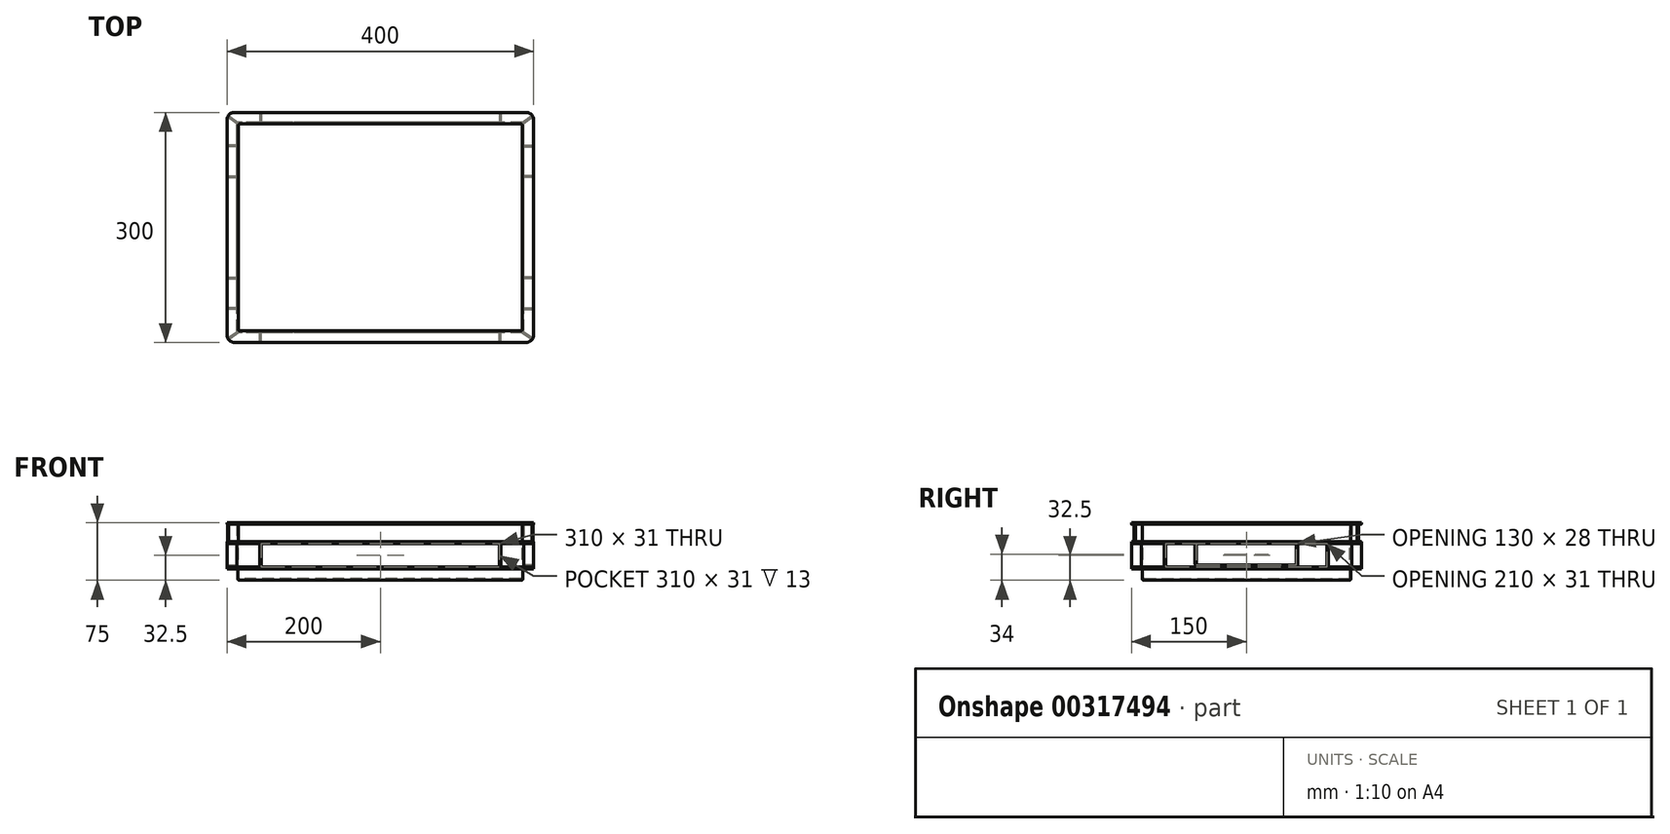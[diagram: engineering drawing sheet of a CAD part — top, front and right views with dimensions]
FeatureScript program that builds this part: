
annotation { "Feature Type Name" : "Feature", "Feature Type Description" : "" }
export const myFeature = defineFeature(function(context is Context, id is Id, definition is map)
    precondition{}
    {
        {
            var Q0;
            Q0=qCreatedBy(makeId("Top.planeOp"),FACE);
            var sketch = newSketch(context, id + "F0", { "sketchPlane" : qUnion([Q0])});
            skLineSegment(sketch, "E0.bottom", {"start": v(186, -136) * mm, "end": v(-186, -136) * mm});
            skLineSegment(sketch, "E0.top", {"start": v(186, 136) * mm, "end": v(-186, 136) * mm});
            skLineSegment(sketch, "E0.left", {"start": v(186, -136) * mm, "end": v(186, 136) * mm});
            skLineSegment(sketch, "E0.right", {"start": v(-186, -136) * mm, "end": v(-186, 136) * mm});
            skPoint(sketch, "E0.middle", {"position": v(0, 0) * mm});
            skPoint(sketch, "E1.visualSharp", {"position": v(-186, 136) * mm});
            skPoint(sketch, "E2.visualSharp", {"position": v(186, 136) * mm});
            skPoint(sketch, "E3.visualSharp", {"position": v(186, -136) * mm});
            skPoint(sketch, "E4.visualSharp", {"position": v(-186, -136) * mm});
            skSolve(sketch);
        }
        {
            var Q0;
            Q0=qSketchRegion(id+"F0",true);
            extrude(context, id + "F1", {"entities" : qUnion([Q0]), "depth" : 15 * mm});
        }
        {
            var Q0;
            Q0=makeQuery(id+"F1.opExtrude","CAP_FACE",FACE,{"disambiguationData":[OSD([sQuery(id+"F0.wireOp",EDGE,"E0.bottom"),sQuery(id+"F0.wireOp",EDGE,"E0.top"),sQuery(id+"F0.wireOp",EDGE,"E0.left"),sQuery(id+"F0.wireOp",EDGE,"E0.right")])],"isStart":false});
            var sketch = newSketch(context, id + "F2", { "sketchPlane" : qUnion([Q0])});
            skLineSegment(sketch, "E5.bottom", {"start": v(190, -150) * mm, "end": v(-190, -150) * mm});
            skLineSegment(sketch, "E5.top", {"start": v(190, 150) * mm, "end": v(-190, 150) * mm});
            skLineSegment(sketch, "E5.left", {"start": v(200, -140) * mm, "end": v(200, 140) * mm});
            skLineSegment(sketch, "E5.right", {"start": v(-200, -140) * mm, "end": v(-200, 140) * mm});
            skPoint(sketch, "E5.middle", {"position": v(0, 0) * mm});
            skPoint(sketch, "E6.visualSharp", {"position": v(-200, 150) * mm});
            skArc(sketch, "E6.filletArc", {"start": v(-190, 150) * mm, "mid": v(-197.07, 147.07) * mm, "end": v(-200, 140) * mm});
            skPoint(sketch, "E7.visualSharp", {"position": v(200, 150) * mm});
            skArc(sketch, "E7.filletArc", {"start": v(200, 140) * mm, "mid": v(197.07, 147.07) * mm, "end": v(190, 150) * mm});
            skPoint(sketch, "E8.visualSharp", {"position": v(200, -150) * mm});
            skArc(sketch, "E8.filletArc", {"start": v(190, -150) * mm, "mid": v(197.07, -147.07) * mm, "end": v(200, -140) * mm});
            skPoint(sketch, "E9.visualSharp", {"position": v(-200, -150) * mm});
            skArc(sketch, "E9.filletArc", {"start": v(-200, -140) * mm, "mid": v(-197.07, -147.07) * mm, "end": v(-190, -150) * mm});
            skSolve(sketch);
        }
        {
            var Q0;
            Q0=makeQuery(id+"F2.imprint","IMPRINT",FACE,{"disambiguationData":[TD([[makeQuery(id+"F2.imprint","IMPRINT",EDGE,{"derivedFrom":makeQuery(id+"F1.opExtrude","CAP_EDGE",EDGE,{"disambiguationData":[OSD([sQuery(id+"F0.wireOp",EDGE,"E0.bottom")])],"isStart":false})}),-1.0]])]});
            var Q1;
            Q1=makeQuery(id+"F2.imprint","IMPRINT",FACE,{"disambiguationData":[TD([[makeQuery(id+"F2.imprint","IMPRINT",EDGE,{"derivedFrom":sQuery(id+"F2.wireOp",EDGE,"E5.bottom")}),-1.0]])]});
            extrude(context, id + "F3", {"entities" : qUnion([Q0, Q1]), "operationType" : NewBodyOperationType.ADD, "depth" : 2 * mm});
        }
        {
            var Q0;
            Q0=makeQuery(id+"F3.opExtrude","CAP_FACE",FACE,{"disambiguationData":[OSD([sQuery(id+"F2.wireOp",EDGE,"E5.bottom"),sQuery(id+"F2.wireOp",EDGE,"E5.top"),sQuery(id+"F2.wireOp",EDGE,"E5.left"),sQuery(id+"F2.wireOp",EDGE,"E5.right"),sQuery(id+"F2.wireOp",EDGE,"E6.filletArc"),sQuery(id+"F2.wireOp",EDGE,"E7.filletArc"),sQuery(id+"F2.wireOp",EDGE,"E8.filletArc"),sQuery(id+"F2.wireOp",EDGE,"E9.filletArc")])],"isStart":false});
            var sketch = newSketch(context, id + "F4", { "sketchPlane" : qUnion([Q0])});
            skLineSegment(sketch, "E10.bottom", {"start": v(187, -137) * mm, "end": v(157, -137) * mm});
            skLineSegment(sketch, "E10.top", {"start": v(187, 137) * mm, "end": v(157, 137) * mm});
            skLineSegment(sketch, "E10.left", {"start": v(187, -137) * mm, "end": v(187, -107) * mm});
            skLineSegment(sketch, "E10.right", {"start": v(-187, -137) * mm, "end": v(-187, -107) * mm});
            skPoint(sketch, "E10.middle", {"position": v(0, 0) * mm});
            skLineSegment(sketch, "E11.bottom", {"start": v(-155, -150) * mm, "end": v(-157, -150) * mm});
            skLineSegment(sketch, "E11.left", {"start": v(-155, -150) * mm, "end": v(-155, -137) * mm});
            skLineSegment(sketch, "E11.right", {"start": v(-157, -150) * mm, "end": v(-157, -137) * mm});
            skPoint(sketch, "E11.middle", {"position": v(-156, -143.5) * mm});
            skLineSegment(sketch, "E12.trimOffspring", {"start": v(-157, -137) * mm, "end": v(-187, -137) * mm});
            skLineSegment(sketch, "E13.bottom", {"start": v(-187, -107) * mm, "end": v(-200, -107) * mm});
            skLineSegment(sketch, "E13.top", {"start": v(-187, -105) * mm, "end": v(-200, -105) * mm});
            skLineSegment(sketch, "E13.right", {"start": v(-200, -107) * mm, "end": v(-200, -105) * mm});
            skPoint(sketch, "E13.middle", {"position": v(-193.5, -106) * mm});
            skLineSegment(sketch, "E14.trimOffspring", {"start": v(-187, -105) * mm, "end": v(-187, 105) * mm});
            skLineSegment(sketch, "E15.MirrorCS", {"start": v(200, -107) * mm, "end": v(200, -105) * mm});
            skLineSegment(sketch, "E16.MirrorCS", {"start": v(155, -150) * mm, "end": v(155, -137) * mm});
            skLineSegment(sketch, "E17.MirrorCS", {"start": v(155, -150) * mm, "end": v(157, -150) * mm});
            skLineSegment(sketch, "E18.MirrorCS", {"start": v(157, -150) * mm, "end": v(157, -137) * mm});
            skLineSegment(sketch, "E19.MirrorCS", {"start": v(187, -105) * mm, "end": v(200, -105) * mm});
            skLineSegment(sketch, "E20.MirrorCS", {"start": v(187, -107) * mm, "end": v(200, -107) * mm});
            skPoint(sketch, "E21.MirrorP", {"position": v(193.5, -106) * mm});
            skLineSegment(sketch, "E22.trimOffspring", {"start": v(187, -105) * mm, "end": v(187, 105) * mm});
            skLineSegment(sketch, "E23.trimOffspring", {"start": v(155, -137) * mm, "end": v(-155, -137) * mm});
            skLineSegment(sketch, "E24.MirrorCS", {"start": v(-200, 107) * mm, "end": v(-200, 105) * mm});
            skPoint(sketch, "E25.MirrorP", {"position": v(-193.5, 106) * mm});
            skLineSegment(sketch, "E26.MirrorCS", {"start": v(-187, 105) * mm, "end": v(-200, 105) * mm});
            skLineSegment(sketch, "E27.MirrorCS", {"start": v(-187, 107) * mm, "end": v(-200, 107) * mm});
            skLineSegment(sketch, "E28.MirrorCS", {"start": v(-155, 150) * mm, "end": v(-157, 150) * mm});
            skLineSegment(sketch, "E29.MirrorCS", {"start": v(-157, 150) * mm, "end": v(-157, 137) * mm});
            skPoint(sketch, "E30.MirrorP", {"position": v(-156, 143.5) * mm});
            skLineSegment(sketch, "E31.MirrorCS", {"start": v(-155, 150) * mm, "end": v(-155, 137) * mm});
            skLineSegment(sketch, "E32.MirrorCS", {"start": v(155, 150) * mm, "end": v(157, 150) * mm});
            skLineSegment(sketch, "E33.MirrorCS", {"start": v(155, 150) * mm, "end": v(155, 137) * mm});
            skLineSegment(sketch, "E34.MirrorCS", {"start": v(157, 150) * mm, "end": v(157, 137) * mm});
            skLineSegment(sketch, "E35.MirrorCS", {"start": v(200, 107) * mm, "end": v(200, 105) * mm});
            skLineSegment(sketch, "E36.MirrorCS", {"start": v(187, 105) * mm, "end": v(200, 105) * mm});
            skPoint(sketch, "E37.MirrorP", {"position": v(193.5, 106) * mm});
            skLineSegment(sketch, "E38.MirrorCS", {"start": v(187, 107) * mm, "end": v(200, 107) * mm});
            skLineSegment(sketch, "E39.trimOffspring", {"start": v(-187, 107) * mm, "end": v(-187, 137) * mm});
            skLineSegment(sketch, "E40.trimOffspring", {"start": v(-157, 137) * mm, "end": v(-187, 137) * mm});
            skLineSegment(sketch, "E41.trimOffspring", {"start": v(155, 137) * mm, "end": v(-155, 137) * mm});
            skLineSegment(sketch, "E42.trimOffspring", {"start": v(187, 107) * mm, "end": v(187, 137) * mm});
            skSolve(sketch);
        }
        {
            var Q0;
            Q0=qSketchRegion(id+"F4",true);
            extrude(context, id + "F5", {"entities" : qUnion([Q0]), "operationType" : NewBodyOperationType.ADD, "depth" : ((126 - 50) - 45) * mm});
        }
        {
            var Q0;
            Q0=makeQuery(id+"F5.opExtrude","CAP_FACE",FACE,{"disambiguationData":[OSD([sQuery(id+"F4.wireOp",EDGE,"E10.bottom"),sQuery(id+"F4.wireOp",EDGE,"E10.top"),sQuery(id+"F4.wireOp",EDGE,"E10.left"),sQuery(id+"F4.wireOp",EDGE,"E10.right")])],"isStart":false});
            var sketch = newSketch(context, id + "F6", { "sketchPlane" : qUnion([Q0])});
            skArc(sketch, "E43.0", {"start": v(-190, 150) * mm, "mid": v(-197.07, 147.07) * mm, "end": v(-200, 140) * mm});
            skArc(sketch, "E43.1", {"start": v(-200, -140) * mm, "mid": v(-197.07, -147.07) * mm, "end": v(-190, -150) * mm});
            skArc(sketch, "E43.2", {"start": v(190, -150) * mm, "mid": v(197.07, -147.07) * mm, "end": v(200, -140) * mm});
            skArc(sketch, "E43.3", {"start": v(200, 140) * mm, "mid": v(197.07, 147.07) * mm, "end": v(190, 150) * mm});
            skLineSegment(sketch, "E44", {"start": v(-200, 140) * mm, "end": v(-200, -140) * mm});
            skLineSegment(sketch, "E45", {"start": v(-190, -150) * mm, "end": v(190, -150) * mm});
            skLineSegment(sketch, "E46", {"start": v(200, 140) * mm, "end": v(200, -140) * mm});
            skLineSegment(sketch, "E47", {"start": v(-190, 150) * mm, "end": v(190, 150) * mm});
            skSolve(sketch);
        }
        {
            var Q0;
            Q0=qSketchRegion(id+"F6",true);
            extrude(context, id + "F7", {"entities" : qUnion([Q0]), "operationType" : NewBodyOperationType.ADD, "depth" : 2 * mm});
        }
        {
            var Q0;
            Q0=makeQuery(id+"F7.opExtrude","CAP_FACE",FACE,{"disambiguationData":[OSD([sQuery(id+"F6.wireOp",EDGE,"E43.0"),sQuery(id+"F6.wireOp",EDGE,"E43.1"),sQuery(id+"F6.wireOp",EDGE,"E43.2"),sQuery(id+"F6.wireOp",EDGE,"E43.3"),sQuery(id+"F6.wireOp",EDGE,"E44"),sQuery(id+"F6.wireOp",EDGE,"E45"),sQuery(id+"F6.wireOp",EDGE,"E46"),sQuery(id+"F6.wireOp",EDGE,"E47")])],"isStart":false});
            var sketch = newSketch(context, id + "F8", { "sketchPlane" : qUnion([Q0])});
            skLineSegment(sketch, "E48.bottom", {"start": v(185.3, -137) * mm, "end": v(-185.3, -137) * mm});
            skLineSegment(sketch, "E48.top", {"start": v(185.3, 137) * mm, "end": v(-185.3, 137) * mm});
            skLineSegment(sketch, "E48.left", {"start": v(187, -135.76) * mm, "end": v(187, 135.76) * mm});
            skLineSegment(sketch, "E48.right", {"start": v(-187, -135.76) * mm, "end": v(-187, 135.76) * mm});
            skPoint(sketch, "E48.middle", {"position": v(0, 0) * mm});
            skLineSegment(sketch, "E49", {"start": v(-187, 137) * mm, "end": v(187, -137) * mm, "construction": true});
            skLineSegment(sketch, "E50.0", {"start": v(-198.93, 144.5) * mm, "end": v(-187, 135.76) * mm});
            skLineSegment(sketch, "E51.0", {"start": v(-197.85, 146.2) * mm, "end": v(-185.3, 137) * mm});
            skArc(sketch, "E52.0", {"start": v(-197.85, 146.2) * mm, "mid": v(-198.43, 145.37) * mm, "end": v(-198.93, 144.5) * mm});
            skPoint(sketch, "E53.orphan", {"position": v(-190, 150) * mm});
            skPoint(sketch, "E54.orphan", {"position": v(-200, 140) * mm});
            skArc(sketch, "E55.0", {"start": v(197.85, -146.2) * mm, "mid": v(198.43, -145.37) * mm, "end": v(198.93, -144.5) * mm});
            skPoint(sketch, "E56.orphan", {"position": v(200, -140) * mm});
            skPoint(sketch, "E57.orphan", {"position": v(190, -150) * mm});
            skLineSegment(sketch, "E58.trimOffspring", {"start": v(187, -135.76) * mm, "end": v(198.93, -144.5) * mm});
            skLineSegment(sketch, "E59.trimOffspring", {"start": v(185.3, -137) * mm, "end": v(197.85, -146.2) * mm});
            skLineSegment(sketch, "E60.MirrorCS", {"start": v(-197.85, -146.2) * mm, "end": v(-185.3, -137) * mm});
            skPoint(sketch, "E61.MirrorP", {"position": v(-200, -140) * mm});
            skArc(sketch, "E62.MirrorCS", {"start": v(-197.85, -146.2) * mm, "mid": v(-198.43, -145.37) * mm, "end": v(-198.93, -144.5) * mm});
            skLineSegment(sketch, "E63.MirrorCS", {"start": v(-198.93, -144.5) * mm, "end": v(-187, -135.76) * mm});
            skPoint(sketch, "E64.MirrorP", {"position": v(-190, -150) * mm});
            skArc(sketch, "E65.MirrorCS", {"start": v(197.85, 146.2) * mm, "mid": v(198.43, 145.37) * mm, "end": v(198.93, 144.5) * mm});
            skPoint(sketch, "E66.MirrorP", {"position": v(200, 140) * mm});
            skPoint(sketch, "E67.MirrorP", {"position": v(190, 150) * mm});
            skLineSegment(sketch, "E68.MirrorCS", {"start": v(187, 135.76) * mm, "end": v(198.93, 144.5) * mm});
            skLineSegment(sketch, "E69.MirrorCS", {"start": v(185.3, 137) * mm, "end": v(197.85, 146.2) * mm});
            skPoint(sketch, "E70.orphan", {"position": v(187, 137) * mm});
            skPoint(sketch, "E71.orphan", {"position": v(-187, -137) * mm});
            skSolve(sketch);
        }
        {
            var Q0;
            Q0=qSketchRegion(id+"F8",true);
            extrude(context, id + "F9", {"entities" : qUnion([Q0]), "operationType" : NewBodyOperationType.ADD, "depth" : 23 * mm});
        }
        {
            var Q0;
            Q0=makeQuery(id+"F9.opExtrude","CAP_FACE",FACE,{"disambiguationData":[OSD([sQuery(id+"F8.wireOp",EDGE,"E48.bottom"),sQuery(id+"F8.wireOp",EDGE,"E48.top"),sQuery(id+"F8.wireOp",EDGE,"E48.left"),sQuery(id+"F8.wireOp",EDGE,"E48.right"),sQuery(id+"F8.wireOp",EDGE,"E50.0"),sQuery(id+"F8.wireOp",EDGE,"E51.0"),sQuery(id+"F8.wireOp",EDGE,"E52.0"),sQuery(id+"F8.wireOp",EDGE,"E55.0"),sQuery(id+"F8.wireOp",EDGE,"E58.trimOffspring"),sQuery(id+"F8.wireOp",EDGE,"E59.trimOffspring"),sQuery(id+"F8.wireOp",EDGE,"E60.MirrorCS"),sQuery(id+"F8.wireOp",EDGE,"E62.MirrorCS"),sQuery(id+"F8.wireOp",EDGE,"E63.MirrorCS"),sQuery(id+"F8.wireOp",EDGE,"E65.MirrorCS"),sQuery(id+"F8.wireOp",EDGE,"E68.MirrorCS"),sQuery(id+"F8.wireOp",EDGE,"E69.MirrorCS")])],"isStart":false});
            var sketch = newSketch(context, id + "F10", { "sketchPlane" : qUnion([Q0])});
            skArc(sketch, "E72.0", {"start": v(190, -150) * mm, "mid": v(197.07, -147.07) * mm, "end": v(200, -140) * mm});
            skArc(sketch, "E73.0", {"start": v(-200, -140) * mm, "mid": v(-197.07, -147.07) * mm, "end": v(-190, -150) * mm});
            skArc(sketch, "E74.0", {"start": v(200, 140) * mm, "mid": v(197.07, 147.07) * mm, "end": v(190, 150) * mm});
            skLineSegment(sketch, "E75.0", {"start": v(200, -140) * mm, "end": v(200, 140) * mm});
            skLineSegment(sketch, "E76.0", {"start": v(190, 150) * mm, "end": v(-190, 150) * mm});
            skLineSegment(sketch, "E77.0", {"start": v(190, -150) * mm, "end": v(-190, -150) * mm});
            skLineSegment(sketch, "E78.0", {"start": v(-200, -140) * mm, "end": v(-200, 140) * mm});
            skArc(sketch, "E79.0", {"start": v(-190, 150) * mm, "mid": v(-197.07, 147.07) * mm, "end": v(-200, 140) * mm});
            skSolve(sketch);
        }
        {
            var Q0;
            Q0=qSketchRegion(id+"F10",true);
            extrude(context, id + "F11", {"entities" : qUnion([Q0]), "operationType" : NewBodyOperationType.ADD, "depth" : 2 * mm});
        }
        {
            var Q0;
            Q0=makeQuery(id+"F11.opExtrude","CAP_FACE",FACE,{"disambiguationData":[OSD([sQuery(id+"F10.wireOp",EDGE,"E72.0"),sQuery(id+"F10.wireOp",EDGE,"E73.0"),sQuery(id+"F10.wireOp",EDGE,"E74.0"),sQuery(id+"F10.wireOp",EDGE,"E75.0"),sQuery(id+"F10.wireOp",EDGE,"E76.0"),sQuery(id+"F10.wireOp",EDGE,"E77.0"),sQuery(id+"F10.wireOp",EDGE,"E78.0"),sQuery(id+"F10.wireOp",EDGE,"E79.0")])],"isStart":false});
            var sketch = newSketch(context, id + "F12", { "sketchPlane" : qUnion([Q0])});
            skLineSegment(sketch, "E80.bottom", {"start": v(185, -135) * mm, "end": v(-185, -135) * mm});
            skLineSegment(sketch, "E80.top", {"start": v(185, 135) * mm, "end": v(-185, 135) * mm});
            skLineSegment(sketch, "E80.left", {"start": v(185, -135) * mm, "end": v(185, 135) * mm});
            skLineSegment(sketch, "E80.right", {"start": v(-185, -135) * mm, "end": v(-185, 135) * mm});
            skPoint(sketch, "E80.middle", {"position": v(0, 0) * mm});
            skSolve(sketch);
        }
        {
            var Q0;
            Q0=qSketchRegion(id+"F12",true);
            extrude(context, id + "F13", {"entities" : qUnion([Q0]), "operationType" : NewBodyOperationType.REMOVE, "oppositeDirection" : true, "depth" : (168 - 50 - 45) * mm});
        }
        {
            var Q0;
            Q0=makeQuery(id+"F5.opExtrude","SWEPT_FACE",FACE,{"disambiguationData":[OSD([sQuery(id+"F4.wireOp",EDGE,"E14.trimOffspring")])]});
            var sketch = newSketch(context, id + "F14", { "sketchPlane" : qUnion([Q0])});
            skLineSegment(sketch, "E81.bottom", {"start": v(63, 18) * mm, "end": v(-63, 18) * mm});
            skLineSegment(sketch, "E81.left", {"start": v(67, 22) * mm, "end": v(67, 48) * mm});
            skLineSegment(sketch, "E81.right", {"start": v(-67, 22) * mm, "end": v(-67, 48) * mm});
            skPoint(sketch, "E81.middle", {"position": v(0, 70.63) * mm});
            skLineSegment(sketch, "E82.bottom", {"start": v(63, 20) * mm, "end": v(-63, 20) * mm});
            skLineSegment(sketch, "E82.left", {"start": v(65, 22) * mm, "end": v(65, 48) * mm});
            skLineSegment(sketch, "E82.right", {"start": v(-65, 22) * mm, "end": v(-65, 48) * mm});
            skLineSegment(sketch, "E83.0", {"start": v(-67, 48) * mm, "end": v(-65, 48) * mm});
            skPoint(sketch, "E84.orphan", {"position": v(-67, 123.26) * mm});
            skPoint(sketch, "E85.orphan", {"position": v(-65, 121.26) * mm});
            skPoint(sketch, "E86.orphan", {"position": v(65, 121.26) * mm});
            skPoint(sketch, "E87.orphan", {"position": v(67, 123.26) * mm});
            skLineSegment(sketch, "E88.trimOffspring", {"start": v(65, 48) * mm, "end": v(67, 48) * mm});
            skPoint(sketch, "E89.orphan", {"position": v(-105, 48) * mm});
            skPoint(sketch, "E90.orphan", {"position": v(105, 48) * mm});
            skPoint(sketch, "E91.visualSharp", {"position": v(-67, 18) * mm});
            skArc(sketch, "E91.filletArc", {"start": v(-67, 22) * mm, "mid": v(-65.83, 19.17) * mm, "end": v(-63, 18) * mm});
            skPoint(sketch, "E92.visualSharp", {"position": v(67, 18) * mm});
            skArc(sketch, "E92.filletArc", {"start": v(63, 18) * mm, "mid": v(65.83, 19.17) * mm, "end": v(67, 22) * mm});
            skPoint(sketch, "E93.visualSharp", {"position": v(65, 20) * mm});
            skArc(sketch, "E93.filletArc", {"start": v(63, 20) * mm, "mid": v(64.41, 20.59) * mm, "end": v(65, 22) * mm});
            skPoint(sketch, "E94.visualSharp", {"position": v(-65, 20) * mm});
            skArc(sketch, "E94.filletArc", {"start": v(-65, 22) * mm, "mid": v(-64.41, 20.59) * mm, "end": v(-63, 20) * mm});
            skSolve(sketch);
        }
        {
            var Q0;
            Q0=qSketchRegion(id+"F14",true);
            var Q1;
            Q1=makeQuery(id+"F7.boolean.opBoolean","MERGE",FACE,{"derivedFrom":[makeQuery(id+"F5.boolean.opBoolean","MERGE",FACE,{"derivedFrom":[makeQuery(id+"F3.opExtrude","SWEPT_FACE",FACE,{"disambiguationData":[OSD([sQuery(id+"F2.wireOp",EDGE,"E5.right")])]}),makeQuery(id+"F5.opExtrude","SWEPT_FACE",FACE,{"disambiguationData":[OSD([sQuery(id+"F4.wireOp",EDGE,"E13.right")])]}),makeQuery(id+"F5.opExtrude","SWEPT_FACE",FACE,{"disambiguationData":[OSD([sQuery(id+"F4.wireOp",EDGE,"E24.MirrorCS")])]})]}),makeQuery(id+"F7.opExtrude","SWEPT_FACE",FACE,{"disambiguationData":[OSD([sQuery(id+"F6.wireOp",EDGE,"E44")])]})]});
            extrude(context, id + "F15", {"entities" : qUnion([Q0]), "operationType" : NewBodyOperationType.ADD, "endBound" : BoundingType.UP_TO_SURFACE, "endBoundEntityFace" : qUnion([Q1]), "depth" : 25 * mm});
        }
        {
            var Q0;
            Q0=makeQuery(id+"F5.opExtrude","SWEPT_FACE",FACE,{"disambiguationData":[OSD([sQuery(id+"F4.wireOp",EDGE,"E22.trimOffspring")])]});
            var sketch = newSketch(context, id + "F16", { "sketchPlane" : qUnion([Q0])});
            skLineSegment(sketch, "E95.0", {"start": v(67, 22) * mm, "end": v(67, 48) * mm});
            skArc(sketch, "E95.1", {"start": v(67, 22) * mm, "mid": v(65.83, 19.17) * mm, "end": v(63, 18) * mm});
            skLineSegment(sketch, "E95.2", {"start": v(-63, 18) * mm, "end": v(63, 18) * mm});
            skLineSegment(sketch, "E95.3", {"start": v(-63, 20) * mm, "end": v(63, 20) * mm});
            skLineSegment(sketch, "E95.4", {"start": v(65, 22) * mm, "end": v(65, 48) * mm});
            skArc(sketch, "E95.5", {"start": v(65, 22) * mm, "mid": v(64.41, 20.59) * mm, "end": v(63, 20) * mm});
            skArc(sketch, "E95.6", {"start": v(-63, 20) * mm, "mid": v(-64.41, 20.59) * mm, "end": v(-65, 22) * mm});
            skArc(sketch, "E95.7", {"start": v(-63, 18) * mm, "mid": v(-65.83, 19.17) * mm, "end": v(-67, 22) * mm});
            skLineSegment(sketch, "E95.8", {"start": v(-67, 22) * mm, "end": v(-67, 48) * mm});
            skLineSegment(sketch, "E95.9", {"start": v(-65, 22) * mm, "end": v(-65, 48) * mm});
            skLineSegment(sketch, "E96", {"start": v(67, 48) * mm, "end": v(65, 48) * mm});
            skLineSegment(sketch, "E97", {"start": v(-65, 48) * mm, "end": v(-67, 48) * mm});
            skSolve(sketch);
        }
        {
            var Q0;
            Q0=qSketchRegion(id+"F16",true);
            var Q1;
            Q1=makeQuery(id+"F7.boolean.opBoolean","MERGE",FACE,{"derivedFrom":[makeQuery(id+"F5.boolean.opBoolean","MERGE",FACE,{"derivedFrom":[makeQuery(id+"F3.opExtrude","SWEPT_FACE",FACE,{"disambiguationData":[OSD([sQuery(id+"F2.wireOp",EDGE,"E5.left")])]}),makeQuery(id+"F5.opExtrude","SWEPT_FACE",FACE,{"disambiguationData":[OSD([sQuery(id+"F4.wireOp",EDGE,"E15.MirrorCS")])]}),makeQuery(id+"F5.opExtrude","SWEPT_FACE",FACE,{"disambiguationData":[OSD([sQuery(id+"F4.wireOp",EDGE,"E35.MirrorCS")])]})]}),makeQuery(id+"F7.opExtrude","SWEPT_FACE",FACE,{"disambiguationData":[OSD([sQuery(id+"F6.wireOp",EDGE,"E46")])]})]});
            extrude(context, id + "F17", {"entities" : qUnion([Q0]), "operationType" : NewBodyOperationType.ADD, "endBound" : BoundingType.UP_TO_SURFACE, "endBoundEntityFace" : qUnion([Q1]), "depth" : 25 * mm});
        }
        {
            var Q0;
            Q0=makeQuery(id+"F13.boolean.opBoolean","COPY",EDGE,{"derivedFrom":makeQuery(id+"F13.opExtrude","SWEPT_EDGE",EDGE,{"disambiguationData":[OSD([sQuery(id+"F12.wireOp",EDGE,"E80.bottom"),sQuery(id+"F12.wireOp",EDGE,"E80.right")])]})});
            var Q1;
            Q1=makeQuery(id+"F13.boolean.opBoolean","COPY",EDGE,{"derivedFrom":makeQuery(id+"F13.opExtrude","SWEPT_EDGE",EDGE,{"disambiguationData":[OSD([sQuery(id+"F12.wireOp",EDGE,"E80.bottom"),sQuery(id+"F12.wireOp",EDGE,"E80.left")])]})});
            var Q2;
            Q2=makeQuery(id+"F13.boolean.opBoolean","COPY",EDGE,{"derivedFrom":makeQuery(id+"F13.opExtrude","SWEPT_EDGE",EDGE,{"disambiguationData":[OSD([sQuery(id+"F12.wireOp",EDGE,"E80.top"),sQuery(id+"F12.wireOp",EDGE,"E80.left")])]})});
            var Q3;
            Q3=makeQuery(id+"F13.boolean.opBoolean","COPY",EDGE,{"derivedFrom":makeQuery(id+"F13.opExtrude","CAP_EDGE",EDGE,{"disambiguationData":[OSD([sQuery(id+"F12.wireOp",EDGE,"E80.top")])],"isStart":false})});
            var Q4;
            Q4=makeQuery(id+"F13.boolean.opBoolean","COPY",EDGE,{"derivedFrom":makeQuery(id+"F13.opExtrude","CAP_EDGE",EDGE,{"disambiguationData":[OSD([sQuery(id+"F12.wireOp",EDGE,"E80.left")])],"isStart":false})});
            var Q5;
            Q5=makeQuery(id+"F13.boolean.opBoolean","COPY",EDGE,{"derivedFrom":makeQuery(id+"F13.opExtrude","CAP_EDGE",EDGE,{"disambiguationData":[OSD([sQuery(id+"F12.wireOp",EDGE,"E80.bottom")])],"isStart":false})});
            var Q6;
            Q6=makeQuery(id+"F13.boolean.opBoolean","COPY",EDGE,{"derivedFrom":makeQuery(id+"F13.opExtrude","CAP_EDGE",EDGE,{"disambiguationData":[OSD([sQuery(id+"F12.wireOp",EDGE,"E80.right")])],"isStart":false})});
            var Q7;
            Q7=makeQuery(id+"F13.boolean.opBoolean","COPY",EDGE,{"derivedFrom":makeQuery(id+"F13.opExtrude","SWEPT_EDGE",EDGE,{"disambiguationData":[OSD([sQuery(id+"F12.wireOp",EDGE,"E80.top"),sQuery(id+"F12.wireOp",EDGE,"E80.right")])]})});
            var Q8;
            Q8=makeQuery(id+"F5.opExtrude","SWEPT_EDGE",EDGE,{"disambiguationData":[OSD([sQuery(id+"F4.wireOp",EDGE,"E10.bottom"),sQuery(id+"F4.wireOp",EDGE,"E10.left")])]});
            var Q9;
            Q9=makeQuery(id+"F5.opExtrude","SWEPT_EDGE",EDGE,{"disambiguationData":[OSD([sQuery(id+"F4.wireOp",EDGE,"E10.top"),sQuery(id+"F4.wireOp",EDGE,"E42.trimOffspring")])]});
            var Q10;
            Q10=makeQuery(id+"F5.opExtrude","SWEPT_EDGE",EDGE,{"disambiguationData":[OSD([sQuery(id+"F4.wireOp",EDGE,"E39.trimOffspring"),sQuery(id+"F4.wireOp",EDGE,"E40.trimOffspring")])]});
            var Q11;
            Q11=makeQuery(id+"F5.opExtrude","SWEPT_EDGE",EDGE,{"disambiguationData":[OSD([sQuery(id+"F4.wireOp",EDGE,"E10.right"),sQuery(id+"F4.wireOp",EDGE,"E12.trimOffspring")])]});
            var Q12;
            Q12=makeQuery(id+"F1.opExtrude","CAP_EDGE",EDGE,{"disambiguationData":[OSD([sQuery(id+"F0.wireOp",EDGE,"E0.left")])],"isStart":true});
            var Q13;
            Q13=makeQuery(id+"F1.opExtrude","CAP_EDGE",EDGE,{"disambiguationData":[OSD([sQuery(id+"F0.wireOp",EDGE,"E0.top")])],"isStart":true});
            var Q14;
            Q14=makeQuery(id+"F1.opExtrude","SWEPT_EDGE",EDGE,{"disambiguationData":[OSD([sQuery(id+"F0.wireOp",EDGE,"E0.top"),sQuery(id+"F0.wireOp",EDGE,"E0.left")])]});
            var Q15;
            Q15=makeQuery(id+"F1.opExtrude","CAP_EDGE",EDGE,{"disambiguationData":[OSD([sQuery(id+"F0.wireOp",EDGE,"E0.bottom")])],"isStart":true});
            var Q16;
            Q16=makeQuery(id+"F1.opExtrude","SWEPT_EDGE",EDGE,{"disambiguationData":[OSD([sQuery(id+"F0.wireOp",EDGE,"E0.bottom"),sQuery(id+"F0.wireOp",EDGE,"E0.left")])]});
            var Q17;
            Q17=makeQuery(id+"F1.opExtrude","SWEPT_EDGE",EDGE,{"disambiguationData":[OSD([sQuery(id+"F0.wireOp",EDGE,"E0.bottom"),sQuery(id+"F0.wireOp",EDGE,"E0.right")])]});
            var Q18;
            Q18=makeQuery(id+"F1.opExtrude","CAP_EDGE",EDGE,{"disambiguationData":[OSD([sQuery(id+"F0.wireOp",EDGE,"E0.right")])],"isStart":true});
            var Q19;
            Q19=makeQuery(id+"F1.opExtrude","SWEPT_EDGE",EDGE,{"disambiguationData":[OSD([sQuery(id+"F0.wireOp",EDGE,"E0.top"),sQuery(id+"F0.wireOp",EDGE,"E0.right")])]});
            fillet(context, id + "F18", {"entities" : qUnion([Q0, Q1, Q2, Q3, Q4, Q5, Q6, Q7, Q8, Q9, Q10, Q11, Q12, Q13, Q14, Q15, Q16, Q17, Q18, Q19]), "radius" : 2 * mm, "tangentPropagation" : true, "allowEdgeOverflow" : false});
        }
    });
